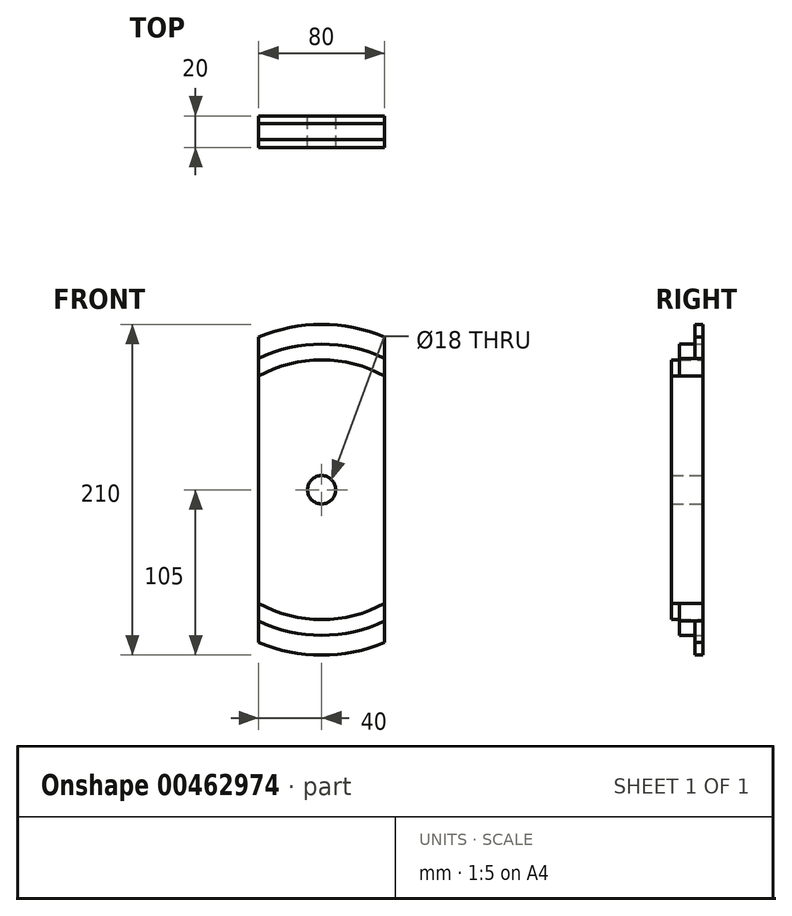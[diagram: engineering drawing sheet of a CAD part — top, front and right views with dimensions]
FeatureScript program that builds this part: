
annotation { "Feature Type Name" : "Feature", "Feature Type Description" : "" }
export const myFeature = defineFeature(function(context is Context, id is Id, definition is map)
    precondition{}
    {
        {
            var Q0;
            Q0=qCreatedBy(makeId("Front.planeOp"),FACE);
            var sketch = newSketch(context, id + "F0", { "sketchPlane" : qUnion([Q0])});
            skCircle(sketch, "E0", {"center": v(0, 0) * mm, "radius": 105 * mm});
            skCircle(sketch, "E1", {"center": v(0, 0) * mm, "radius": 82.5 * mm});
            skCircle(sketch, "E2", {"center": v(0, 0) * mm, "radius": 92.5 * mm});
            skCircle(sketch, "E3", {"center": v(0, 0) * mm, "radius": 9 * mm});
            skLineSegment(sketch, "E4.bottom", {"start": v(-40, 123.24) * mm, "end": v(40, 123.24) * mm});
            skLineSegment(sketch, "E4.top", {"start": v(-40, -119.89) * mm, "end": v(40, -119.89) * mm});
            skLineSegment(sketch, "E4.left", {"start": v(-40, 123.24) * mm, "end": v(-40, -119.89) * mm});
            skLineSegment(sketch, "E4.right", {"start": v(40, 123.24) * mm, "end": v(40, -119.89) * mm});
            skSolve(sketch);
        }
        {
            var Q0;
            {var subQ0=sQuery(id+"F0.wireOp",EDGE,"E4.left");var subQ1=sQuery(id+"F0.wireOp",EDGE,"E0");var subQ2=makeQuery(id+"F0.imprint","INTERSECT",VERTEX,{"disambiguationData":[OD(0.0)],"derivedFrom":[subQ1,subQ0]});Q0=makeQuery(id+"F0.imprint","IMPRINT",FACE,{"disambiguationData":[TD([[makeQuery(id+"F0.imprint","IMPRINT",EDGE,{"disambiguationData":[TD([[subQ2,1.0]])],"derivedFrom":subQ1}),1.0]])]});}
            var Q1;
            {var subQ0=sQuery(id+"F0.wireOp",EDGE,"E4.left");var subQ1=sQuery(id+"F0.wireOp",EDGE,"E0");var subQ2=makeQuery(id+"F0.imprint","INTERSECT",VERTEX,{"disambiguationData":[OD(1.0)],"derivedFrom":[subQ1,subQ0]});Q1=makeQuery(id+"F0.imprint","IMPRINT",FACE,{"disambiguationData":[TD([[makeQuery(id+"F0.imprint","IMPRINT",EDGE,{"disambiguationData":[TD([[subQ2,-1.0]])],"derivedFrom":subQ1}),1.0]])]});}
            extrude(context, id + "F1", {"entities" : qUnion([Q0, Q1]), "depth" : 5 * mm});
        }
        {
            var Q0;
            {var subQ0=sQuery(id+"F0.wireOp",EDGE,"E4.left");var subQ1=sQuery(id+"F0.wireOp",EDGE,"E1");var subQ2=makeQuery(id+"F0.imprint","INTERSECT",VERTEX,{"disambiguationData":[OD(0.0)],"derivedFrom":[subQ1,subQ0]});Q0=makeQuery(id+"F0.imprint","IMPRINT",FACE,{"disambiguationData":[TD([[makeQuery(id+"F0.imprint","IMPRINT",EDGE,{"disambiguationData":[TD([[subQ2,1.0]])],"derivedFrom":subQ1}),-1.0]])]});}
            var Q1;
            {var subQ0=sQuery(id+"F0.wireOp",EDGE,"E4.left");var subQ1=sQuery(id+"F0.wireOp",EDGE,"E1");var subQ2=makeQuery(id+"F0.imprint","INTERSECT",VERTEX,{"disambiguationData":[OD(1.0)],"derivedFrom":[subQ1,subQ0]});Q1=makeQuery(id+"F0.imprint","IMPRINT",FACE,{"disambiguationData":[TD([[makeQuery(id+"F0.imprint","IMPRINT",EDGE,{"disambiguationData":[TD([[subQ2,-1.0]])],"derivedFrom":subQ1}),-1.0]])]});}
            extrude(context, id + "F2", {"entities" : qUnion([Q0, Q1]), "depth" : 15 * mm});
        }
        {
            var Q0;
            Q0=makeQuery(id+"F0.imprint","IMPRINT",FACE,{"disambiguationData":[TD([[makeQuery(id+"F0.imprint","IMPRINT",EDGE,{"derivedFrom":sQuery(id+"F0.wireOp",EDGE,"E3")}),-1.0]])]});
            extrude(context, id + "F3", {"entities" : qUnion([Q0]), "depth" : 20 * mm});
        }
    });
